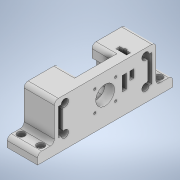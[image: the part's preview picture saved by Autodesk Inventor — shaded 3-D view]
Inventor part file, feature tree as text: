
AUTODESK INVENTOR PART (.ipt)
format: ipt  version: 2020 (Build 240168000, 168)  size: 338,944 bytes
history: native  units: mm
features: extrude x11, sketch x6, projected_geometry x3, other x1, mirror x1
ambient origin geometry x8: Origin, YZ Plane, XZ Plane, XY Plane, X Axis, Y Axis, Z Axis, Center Point
bodies: Body1 (feature_tree)
feature tree (22):
  other  "Bryła1"
  sketch  "Szkic1"
  extrude  "Wyciągnięcie proste1"  Depth=28.0mm
  extrude  "Wyciągnięcie proste2"  Depth=11.0mm
  extrude  "Wyciągnięcie proste12"  Depth=40.0mm
  extrude  "Wyciągnięcie proste4"  Depth=20.0mm
  sketch  "Szkic2"
  extrude  "Wyciągnięcie proste5"  Depth=60.0mm
  extrude  "Wyciągnięcie proste6"  Depth=6.0mm
  mirror  "Odbij1"
  extrude  "Wyciągnięcie proste8"  Depth=3.5mm
  sketch  "Szkic3"
  extrude  "Wyciągnięcie proste7"  TaperAngle=150.0deg  [1 undecoded]
  extrude  "Wyciągnięcie proste9"  TaperAngle=150.0deg  [1 undecoded]
  extrude  "Wyciągnięcie proste10"  Depth=26.0mm
  extrude  "Wyciągnięcie proste11"  Depth=13.0mm
  sketch  "Szkic5"
  projected_geometry  "Pętla rzutowana1"
  sketch  "Szkic6"
  projected_geometry  "Pętla rzutowana2"
  sketch  "Szkic7"
  projected_geometry  "Pętla rzutowana3"
note: 2 required parameter values undecoded (feature->parameter linkage not recoverable at this tier; creation-order binding heuristic only, values carry confidence <= 0.55)
